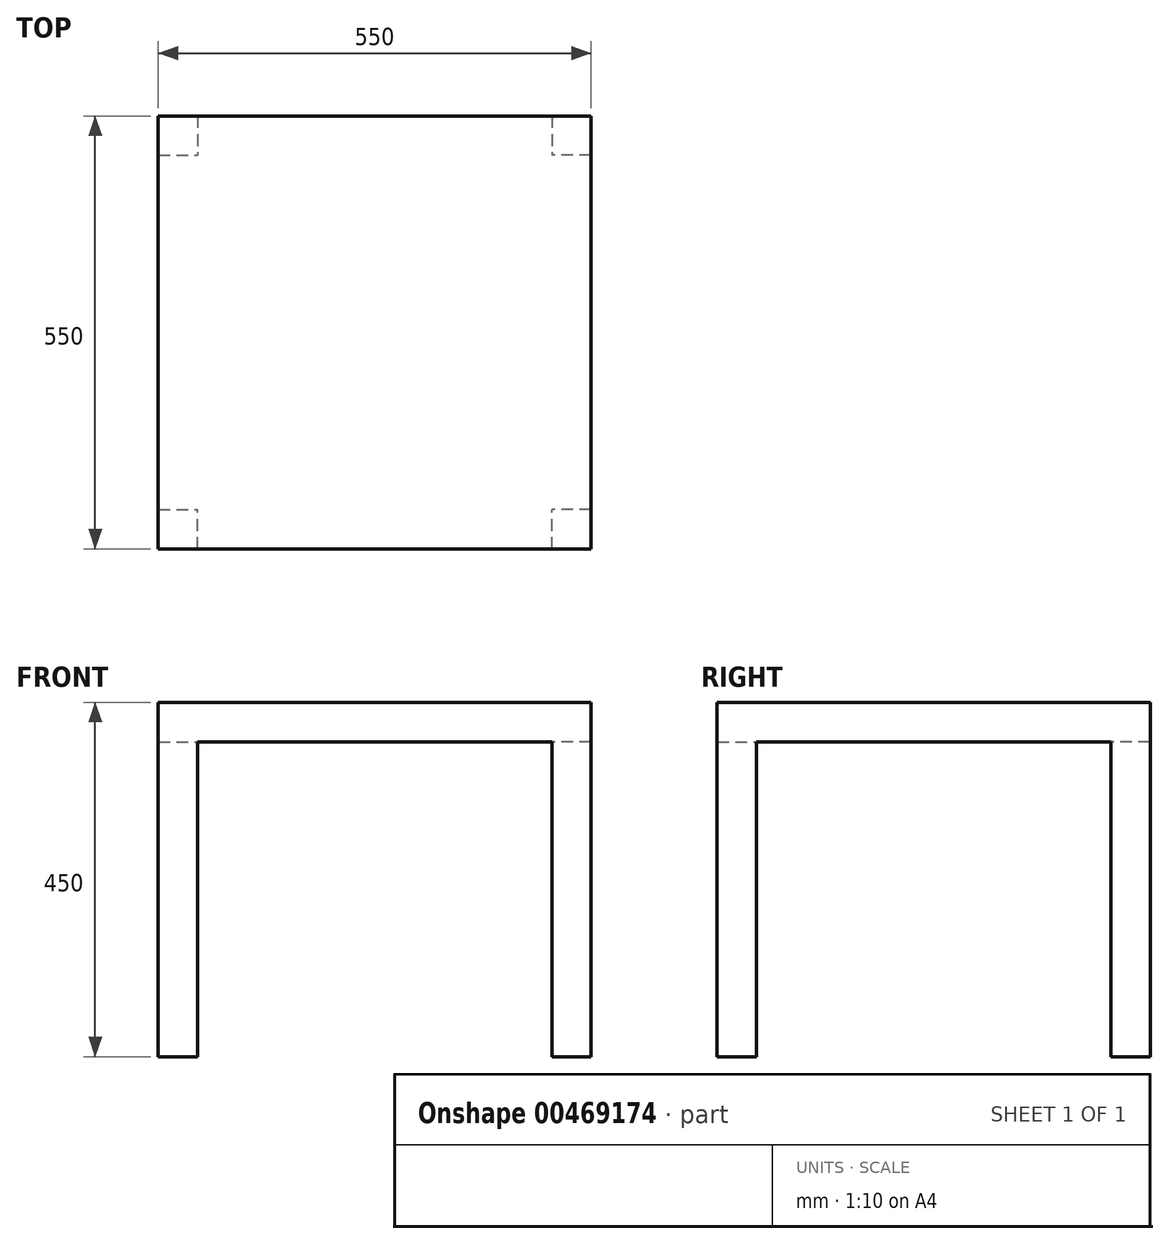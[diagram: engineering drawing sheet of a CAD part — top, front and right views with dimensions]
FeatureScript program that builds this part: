
annotation { "Feature Type Name" : "Feature", "Feature Type Description" : "" }
export const myFeature = defineFeature(function(context is Context, id is Id, definition is map)
    precondition{}
    {
        {
            var Q0;
            Q0=qCreatedBy(makeId("Top.planeOp"),FACE);
            var sketch = newSketch(context, id + "F0", { "sketchPlane" : qUnion([Q0])});
            skLineSegment(sketch, "E0.bottom", {"start": v(0, 550) * mm, "end": v(550, 550) * mm});
            skLineSegment(sketch, "E0.top", {"start": v(0, 0) * mm, "end": v(550, 0) * mm});
            skLineSegment(sketch, "E0.left", {"start": v(0, 550) * mm, "end": v(0, 0) * mm});
            skLineSegment(sketch, "E0.right", {"start": v(550, 550) * mm, "end": v(550, 0) * mm});
            skSolve(sketch);
        }
        {
            var Q0;
            Q0=makeQuery(id+"F0.imprint","IMPRINT",FACE,{"disambiguationData":[TD([[makeQuery(id+"F0.imprint","IMPRINT",EDGE,{"derivedFrom":sQuery(id+"F0.wireOp",EDGE,"E0.bottom")}),-1.0]])]});
            extrude(context, id + "F1", {"entities" : qUnion([Q0]), "oppositeDirection" : true, "depth" : 50 * mm});
        }
        {
            var Q0;
            Q0=makeQuery(id+"F1.opExtrude","CAP_FACE",FACE,{"disambiguationData":[OSD([sQuery(id+"F0.wireOp",EDGE,"E0.bottom"),sQuery(id+"F0.wireOp",EDGE,"E0.top"),sQuery(id+"F0.wireOp",EDGE,"E0.left"),sQuery(id+"F0.wireOp",EDGE,"E0.right")])],"isStart":false});
            var sketch = newSketch(context, id + "F2", { "sketchPlane" : qUnion([Q0])});
            skLineSegment(sketch, "E1.bottom", {"start": v(550, 0) * mm, "end": v(500, 0) * mm});
            skLineSegment(sketch, "E1.top", {"start": v(550, -50) * mm, "end": v(500, -50) * mm});
            skLineSegment(sketch, "E1.left", {"start": v(550, 0) * mm, "end": v(550, -50) * mm});
            skLineSegment(sketch, "E1.right", {"start": v(500, 0) * mm, "end": v(500, -50) * mm});
            skLineSegment(sketch, "E2.bottom", {"start": v(0, 0) * mm, "end": v(50, 0) * mm});
            skLineSegment(sketch, "E2.top", {"start": v(0, -50) * mm, "end": v(50, -50) * mm});
            skLineSegment(sketch, "E2.left", {"start": v(0, 0) * mm, "end": v(0, -50) * mm});
            skLineSegment(sketch, "E2.right", {"start": v(50, 0) * mm, "end": v(50, -50) * mm});
            skLineSegment(sketch, "E3.bottom", {"start": v(0, -550) * mm, "end": v(50, -550) * mm});
            skLineSegment(sketch, "E3.top", {"start": v(0, -500) * mm, "end": v(50, -500) * mm});
            skLineSegment(sketch, "E3.left", {"start": v(0, -550) * mm, "end": v(0, -500) * mm});
            skLineSegment(sketch, "E3.right", {"start": v(50, -550) * mm, "end": v(50, -500) * mm});
            skLineSegment(sketch, "E4.bottom", {"start": v(550, -550) * mm, "end": v(500, -550) * mm});
            skLineSegment(sketch, "E4.top", {"start": v(550, -500) * mm, "end": v(500, -500) * mm});
            skLineSegment(sketch, "E4.left", {"start": v(550, -550) * mm, "end": v(550, -500) * mm});
            skLineSegment(sketch, "E4.right", {"start": v(500, -550) * mm, "end": v(500, -500) * mm});
            skSolve(sketch);
        }
        {
            var Q0;
            Q0=makeQuery(id+"F2.imprint","IMPRINT",FACE,{"disambiguationData":[TD([[makeQuery(id+"F2.imprint","IMPRINT",EDGE,{"derivedFrom":sQuery(id+"F2.wireOp",EDGE,"E1.bottom")}),-1.0]])]});
            var Q1;
            Q1=makeQuery(id+"F2.imprint","IMPRINT",FACE,{"disambiguationData":[TD([[makeQuery(id+"F2.imprint","IMPRINT",EDGE,{"derivedFrom":sQuery(id+"F2.wireOp",EDGE,"E4.bottom")}),1.0]])]});
            var Q2;
            Q2=makeQuery(id+"F2.imprint","IMPRINT",FACE,{"disambiguationData":[TD([[makeQuery(id+"F2.imprint","IMPRINT",EDGE,{"derivedFrom":sQuery(id+"F2.wireOp",EDGE,"E3.bottom")}),1.0]])]});
            var Q3;
            Q3=makeQuery(id+"F2.imprint","IMPRINT",FACE,{"disambiguationData":[TD([[makeQuery(id+"F2.imprint","IMPRINT",EDGE,{"derivedFrom":sQuery(id+"F2.wireOp",EDGE,"E2.bottom")}),-1.0]])]});
            extrude(context, id + "F3", {"entities" : qUnion([Q0, Q1, Q2, Q3]), "operationType" : NewBodyOperationType.ADD, "depth" : 400 * mm});
        }
    });
